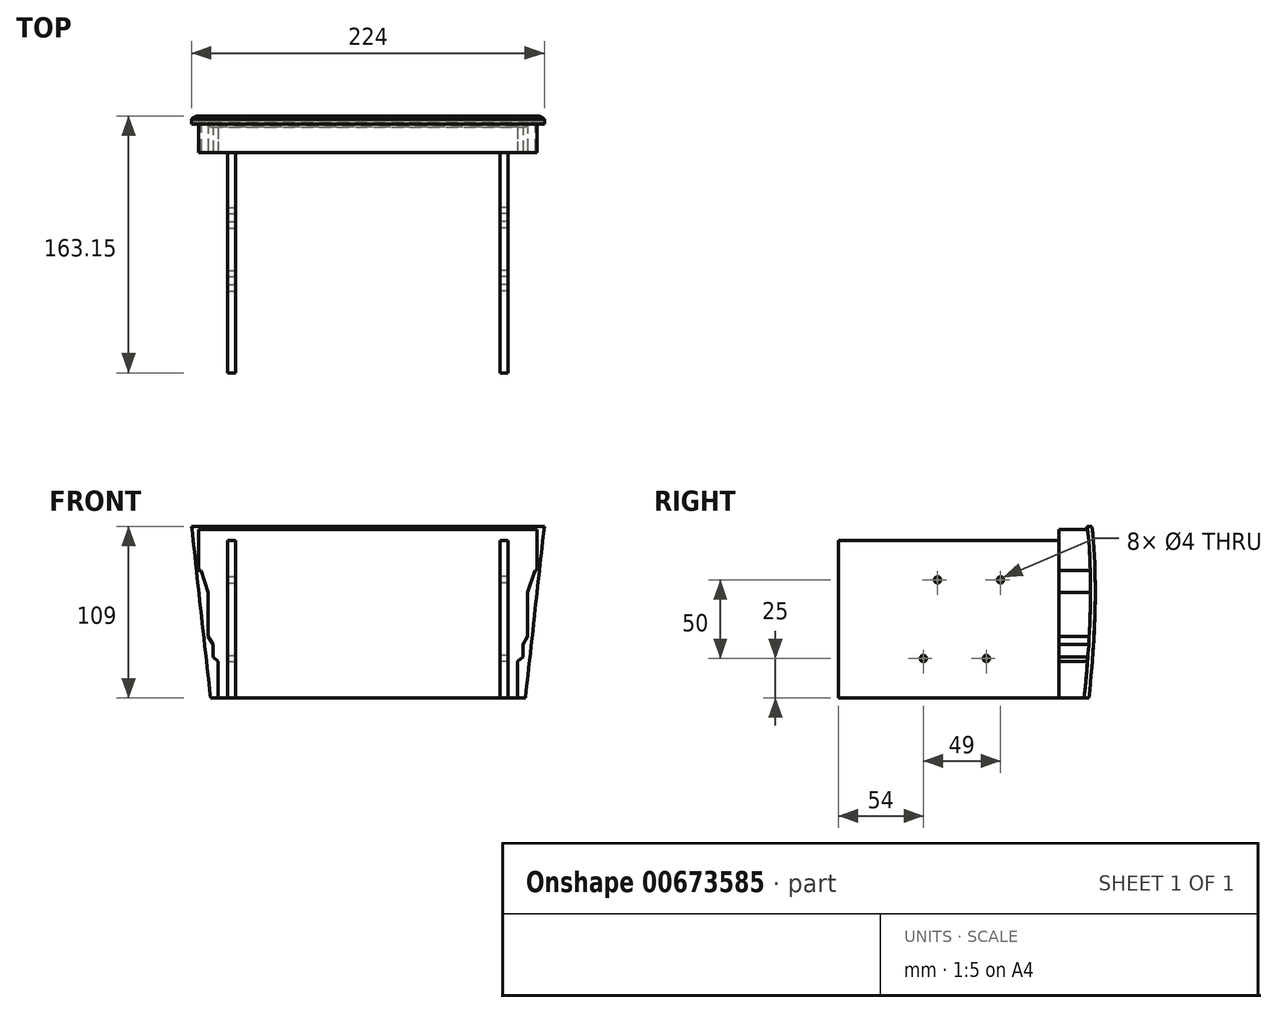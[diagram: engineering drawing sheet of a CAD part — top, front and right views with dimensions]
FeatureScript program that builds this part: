
annotation { "Feature Type Name" : "Feature", "Feature Type Description" : "" }
export const myFeature = defineFeature(function(context is Context, id is Id, definition is map)
    precondition{}
    {
        {
            var Q0;
            Q0=qCreatedBy(makeId("Front.planeOp"),FACE);
            var sketch = newSketch(context, id + "F0", { "sketchPlane" : qUnion([Q0])});
            skLineSegment(sketch, "E0", {"start": v(-165.88, 0) * mm, "end": v(159.26, 0) * mm, "construction": true});
            skLineSegment(sketch, "E1", {"start": v(0, -94.38) * mm, "end": v(0, 198.38) * mm, "construction": true});
            skLineSegment(sketch, "E2", {"start": v(-100, 0) * mm, "end": v(100, 0) * mm});
            skLineSegment(sketch, "E3", {"start": v(100, 0) * mm, "end": v(112, 109) * mm});
            skLineSegment(sketch, "E4", {"start": v(112, 109) * mm, "end": v(-112, 109) * mm});
            skLineSegment(sketch, "E5", {"start": v(-112, 109) * mm, "end": v(-100, 0) * mm});
            skPoint(sketch, "E6", {"position": v(0, 109) * mm});
            skSolve(sketch);
        }
        {
            var Q0;
            Q0=qCreatedBy(makeId("Right.planeOp"),FACE);
            var sketch = newSketch(context, id + "F1", { "sketchPlane" : qUnion([Q0])});
            skLineSegment(sketch, "E7", {"start": v(342.7, 0) * mm, "end": v(-406.84, 0) * mm, "construction": true});
            skLineSegment(sketch, "E8", {"start": v(0, 389.9) * mm, "end": v(0, -460.32) * mm, "construction": true});
            skPoint(sketch, "E9", {"position": v(19, 0) * mm});
            skPoint(sketch, "E10", {"position": v(23, 56) * mm});
            skLineSegment(sketch, "E11", {"start": v(-13.69, 109) * mm, "end": v(74.51, 109) * mm, "construction": true});
            skPoint(sketch, "E12", {"position": v(21, 109) * mm});
            skFitSpline(sketch, "E13", {"points": [v(21, 109) * mm, v(23, 56) * mm, v(19, 0) * mm], "startDerivative": vector(8.56, -61) * mm, "endDerivative": vector(-5.9, -39.54) * mm});
            skPoint(sketch, "E14", {"position": v(18, 109) * mm});
            skFitSpline(sketch, "E15", {"points": [v(18, 109.02) * mm, v(20, 56.02) * mm, v(16, 0.02) * mm], "startDerivative": vector(8.56, -61) * mm, "endDerivative": vector(-5.9, -39.54) * mm});
            skLineSegment(sketch, "E16", {"start": v(16, 0.02) * mm, "end": v(19, 0) * mm});
            skLineSegment(sketch, "E17", {"start": v(18, 109) * mm, "end": v(21, 109) * mm});
            skLineSegment(sketch, "E18", {"start": v(18, 109) * mm, "end": v(0, 107) * mm});
            skLineSegment(sketch, "E19", {"start": v(0, 0) * mm, "end": v(16, 0.02) * mm});
            skLineSegment(sketch, "E20", {"start": v(0, 0) * mm, "end": v(0, 107) * mm});
            skSolve(sketch);
        }
        {
            var Q0;
            Q0=qCreatedBy(makeId("Front.planeOp"),FACE);
            var sketch = newSketch(context, id + "F2", { "sketchPlane" : qUnion([Q0])});
            skLineSegment(sketch, "E21", {"start": v(0, 107) * mm, "end": v(107.5, 107) * mm});
            skLineSegment(sketch, "E22", {"start": v(107.5, 107) * mm, "end": v(107.5, 81) * mm});
            skLineSegment(sketch, "E23", {"start": v(101.5, 67) * mm, "end": v(101.5, 39) * mm});
            skLineSegment(sketch, "E24", {"start": v(101.5, 39) * mm, "end": v(98.5, 34) * mm});
            skLineSegment(sketch, "E25", {"start": v(98.5, 34) * mm, "end": v(98.5, 26) * mm});
            skLineSegment(sketch, "E26", {"start": v(98.5, 26) * mm, "end": v(95, 23) * mm});
            skLineSegment(sketch, "E27", {"start": v(95, 23) * mm, "end": v(95, 0) * mm});
            skLineSegment(sketch, "E28", {"start": v(95, 0) * mm, "end": v(0, 0) * mm});
            skLineSegment(sketch, "E29.MirrorCS", {"start": v(0, 107) * mm, "end": v(-107.5, 107) * mm});
            skLineSegment(sketch, "E30.MirrorCS", {"start": v(-107.5, 107) * mm, "end": v(-107.5, 81) * mm});
            skLineSegment(sketch, "E31.MirrorCS", {"start": v(-101.5, 67) * mm, "end": v(-101.5, 39) * mm});
            skLineSegment(sketch, "E32.MirrorCS", {"start": v(-101.5, 39) * mm, "end": v(-98.5, 34) * mm});
            skLineSegment(sketch, "E33.MirrorCS", {"start": v(-98.5, 34) * mm, "end": v(-98.5, 26) * mm});
            skLineSegment(sketch, "E34.MirrorCS", {"start": v(-98.5, 26) * mm, "end": v(-95, 23) * mm});
            skLineSegment(sketch, "E35.MirrorCS", {"start": v(-95, 23) * mm, "end": v(-95, 0) * mm});
            skLineSegment(sketch, "E36.MirrorCS", {"start": v(-95, 0) * mm, "end": v(0, 0) * mm});
            skLineSegment(sketch, "E37", {"start": v(101.5, 67) * mm, "end": v(106, 81) * mm});
            skLineSegment(sketch, "E38", {"start": v(106, 81) * mm, "end": v(107.5, 81) * mm});
            skLineSegment(sketch, "E39.MirrorCS", {"start": v(-101.5, 67) * mm, "end": v(-106, 81) * mm});
            skLineSegment(sketch, "E40.MirrorCS", {"start": v(-106, 81) * mm, "end": v(-107.5, 81) * mm});
            skSolve(sketch);
        }
        {
            var Q0;
            Q0=makeQuery(id+"F0.imprint","IMPRINT",FACE,{"disambiguationData":[TD([[makeQuery(id+"F0.imprint","IMPRINT",EDGE,{"derivedFrom":sQuery(id+"F0.wireOp",EDGE,"E2")}),1.0]])]});
            extrude(context, id + "F3", {"entities" : qUnion([Q0]), "oppositeDirection" : true, "depth" : 52.2 * mm, "offsetDistance" : 25 * mm});
        }
        {
            var Q0;
            {var subQ2=sQuery(id+"F1.wireOp",EDGE,"E18");Q0=makeQuery(id+"F1.imprint","IMPRINT",FACE,{"disambiguationData":[TD([[makeQuery(id+"F1.imprint","IMPRINT",EDGE,{"derivedFrom":subQ2}),1.0]])]});}
            extrude(context, id + "F4", {"entities" : qUnion([Q0]), "depth" : 226.6 * mm, "offsetDistance" : 25 * mm, "symmetric" : true});
        }
        {
            var Q0;
            Q0=makeQuery(id+"F1.imprint","IMPRINT",FACE,{"disambiguationData":[TD([[makeQuery(id+"F1.imprint","IMPRINT",EDGE,{"derivedFrom":sQuery(id+"F1.wireOp",EDGE,"E13")}),-1.0]])]});
            extrude(context, id + "F5", {"entities" : qUnion([Q0]), "oppositeDirection" : true, "depth" : 288.4 * mm, "offsetDistance" : 25 * mm, "symmetric" : true});
        }
        {
            var Q0;
            Q0 = qSketchRegion(id + "F2", true);
            extrude(context, id + "F6", {"entities" : qUnion([Q0]), "oppositeDirection" : true, "depth" : 30.9 * mm, "offsetDistance" : 25 * mm});
        }
        {
            var Q0;
            Q0=qCreatedBy(makeId("Front.planeOp"),FACE);
            var sketch = newSketch(context, id + "F7", { "sketchPlane" : qUnion([Q0])});
            skLineSegment(sketch, "E41", {"start": v(89, 161.66) * mm, "end": v(89, -47.75) * mm, "construction": true});
            skLineSegment(sketch, "E42.bottom", {"start": v(89, 0) * mm, "end": v(84, 0) * mm});
            skLineSegment(sketch, "E42.top", {"start": v(89, 100) * mm, "end": v(84, 100) * mm});
            skLineSegment(sketch, "E42.left", {"start": v(89, 0) * mm, "end": v(89, 100) * mm});
            skLineSegment(sketch, "E42.right", {"start": v(84, 0) * mm, "end": v(84, 100) * mm});
            skLineSegment(sketch, "E43.MirrorCS", {"start": v(-89, 161.66) * mm, "end": v(-89, -47.75) * mm, "construction": true});
            skSolve(sketch);
        }
        {
            var Q0;
            Q0 = qSketchRegion(id + "F7", true);
            extrude(context, id + "F8", {"entities" : qUnion([Q0]), "depth" : 140 * mm, "offsetDistance" : 25 * mm});
        }
        {
            var Q0;
            Q0=makeQuery(id+"F8.opExtrude","SWEPT_FACE",FACE,{"disambiguationData":[OSD([sQuery(id+"F7.wireOp",EDGE,"E42.left")])]});
            var sketch = newSketch(context, id + "F9", { "sketchPlane" : qUnion([Q0])});
            skLineSegment(sketch, "E44", {"start": v(-90.03, 75) * mm, "end": v(0, 75) * mm, "construction": true});
            skLineSegment(sketch, "E45", {"start": v(-94.64, 25) * mm, "end": v(0, 25) * mm, "construction": true});
            skPoint(sketch, "E46", {"position": v(-77, 75) * mm});
            skPoint(sketch, "E47", {"position": v(-37, 75) * mm});
            skPoint(sketch, "E48", {"position": v(-86, 25) * mm});
            skPoint(sketch, "E49", {"position": v(-46, 25) * mm});
            skSolve(sketch);
        }
        {
            var Q0;
            Q0=sQuery(id+"F9.wireOp",VERTEX,"E48");
            var Q1;
            Q1=sQuery(id+"F9.wireOp",VERTEX,"E49");
            var Q2;
            Q2=sQuery(id+"F9.wireOp",VERTEX,"E47");
            var Q3;
            Q3=sQuery(id+"F9.wireOp",VERTEX,"E46");
            var Q4;
            Q4=makeQuery(id+"F8.opExtrude","SWEPT_BODY",BODY,{"disambiguationData":[OSD([sQuery(id+"F7.wireOp",EDGE,"E42.bottom"),sQuery(id+"F7.wireOp",EDGE,"E42.top"),sQuery(id+"F7.wireOp",EDGE,"E42.left"),sQuery(id+"F7.wireOp",EDGE,"E42.right")])]});
            hole(context, id + "F10", {"style" : HoleStyle.SIMPLE, "endStyle" : HoleEndStyle.THROUGH, "holeDiameter" : 4 * mm, "majorDiameter" : 5 * mm, "isTappedThrough" : true, "tappedDepth" : 12 * mm, "tapClearance" : 3, "locations" : qUnion([Q0, Q1, Q2, Q3]), "scope" : qUnion([Q4])});
        }
        {
            var Q0;
            Q0=makeQuery(id+"F8.opExtrude","SWEPT_BODY",BODY,{"disambiguationData":[OSD([sQuery(id+"F7.wireOp",EDGE,"E42.bottom"),sQuery(id+"F7.wireOp",EDGE,"E42.top"),sQuery(id+"F7.wireOp",EDGE,"E42.left"),sQuery(id+"F7.wireOp",EDGE,"E42.right")])]});
            var Q1;
            Q1=qCreatedBy(makeId("Right.planeOp"),FACE);
            mirror(context, id + "F11", {"entities" : qUnion([Q0]), "mirrorPlane" : qUnion([Q1])});
        }
        {
            var Q0;
            Q0=makeQuery(id+"F5.opExtrude","SWEPT_BODY",BODY,{"disambiguationData":[OSD([sQuery(id+"F1.wireOp",EDGE,"E13"),sQuery(id+"F1.wireOp",EDGE,"E15"),sQuery(id+"F1.wireOp",EDGE,"E16"),sQuery(id+"F1.wireOp",EDGE,"E17")])]});
            var Q1;
            Q1=makeQuery(id+"F3.opExtrude","SWEPT_BODY",BODY,{"disambiguationData":[OSD([sQuery(id+"F0.wireOp",EDGE,"E2"),sQuery(id+"F0.wireOp",EDGE,"E3"),sQuery(id+"F0.wireOp",EDGE,"E4"),sQuery(id+"F0.wireOp",EDGE,"E5")])]});
            booleanBodies(context, id + "F12", {"operationType" : BooleanOperationType.INTERSECTION, "tools" : qUnion([Q0, Q1])});
        }
        {
            var Q0;
            Q0=makeQuery(id+"F4.opExtrude","SWEPT_BODY",BODY,{"disambiguationData":[OSD([sQuery(id+"F1.wireOp",EDGE,"E15"),sQuery(id+"F1.wireOp",EDGE,"E18"),sQuery(id+"F1.wireOp",EDGE,"E19"),sQuery(id+"F1.wireOp",EDGE,"E20")])]});
            var Q1;
            Q1=makeQuery(id+"F6.opExtrude","SWEPT_BODY",BODY,{"disambiguationData":[OSD([sQuery(id+"F2.wireOp",EDGE,"E21"),sQuery(id+"F2.wireOp",EDGE,"E22"),sQuery(id+"F2.wireOp",EDGE,"E23"),sQuery(id+"F2.wireOp",EDGE,"E24"),sQuery(id+"F2.wireOp",EDGE,"E25"),sQuery(id+"F2.wireOp",EDGE,"E26"),sQuery(id+"F2.wireOp",EDGE,"E27"),sQuery(id+"F2.wireOp",EDGE,"E28"),sQuery(id+"F2.wireOp",EDGE,"E29.MirrorCS"),sQuery(id+"F2.wireOp",EDGE,"E30.MirrorCS"),sQuery(id+"F2.wireOp",EDGE,"E31.MirrorCS"),sQuery(id+"F2.wireOp",EDGE,"E32.MirrorCS"),sQuery(id+"F2.wireOp",EDGE,"E33.MirrorCS"),sQuery(id+"F2.wireOp",EDGE,"E34.MirrorCS"),sQuery(id+"F2.wireOp",EDGE,"E35.MirrorCS"),sQuery(id+"F2.wireOp",EDGE,"E36.MirrorCS"),sQuery(id+"F2.wireOp",EDGE,"E37"),sQuery(id+"F2.wireOp",EDGE,"E38"),sQuery(id+"F2.wireOp",EDGE,"E39.MirrorCS"),sQuery(id+"F2.wireOp",EDGE,"E40.MirrorCS")])]});
            booleanBodies(context, id + "F13", {"operationType" : BooleanOperationType.INTERSECTION, "tools" : qUnion([Q0, Q1])});
        }
    });
